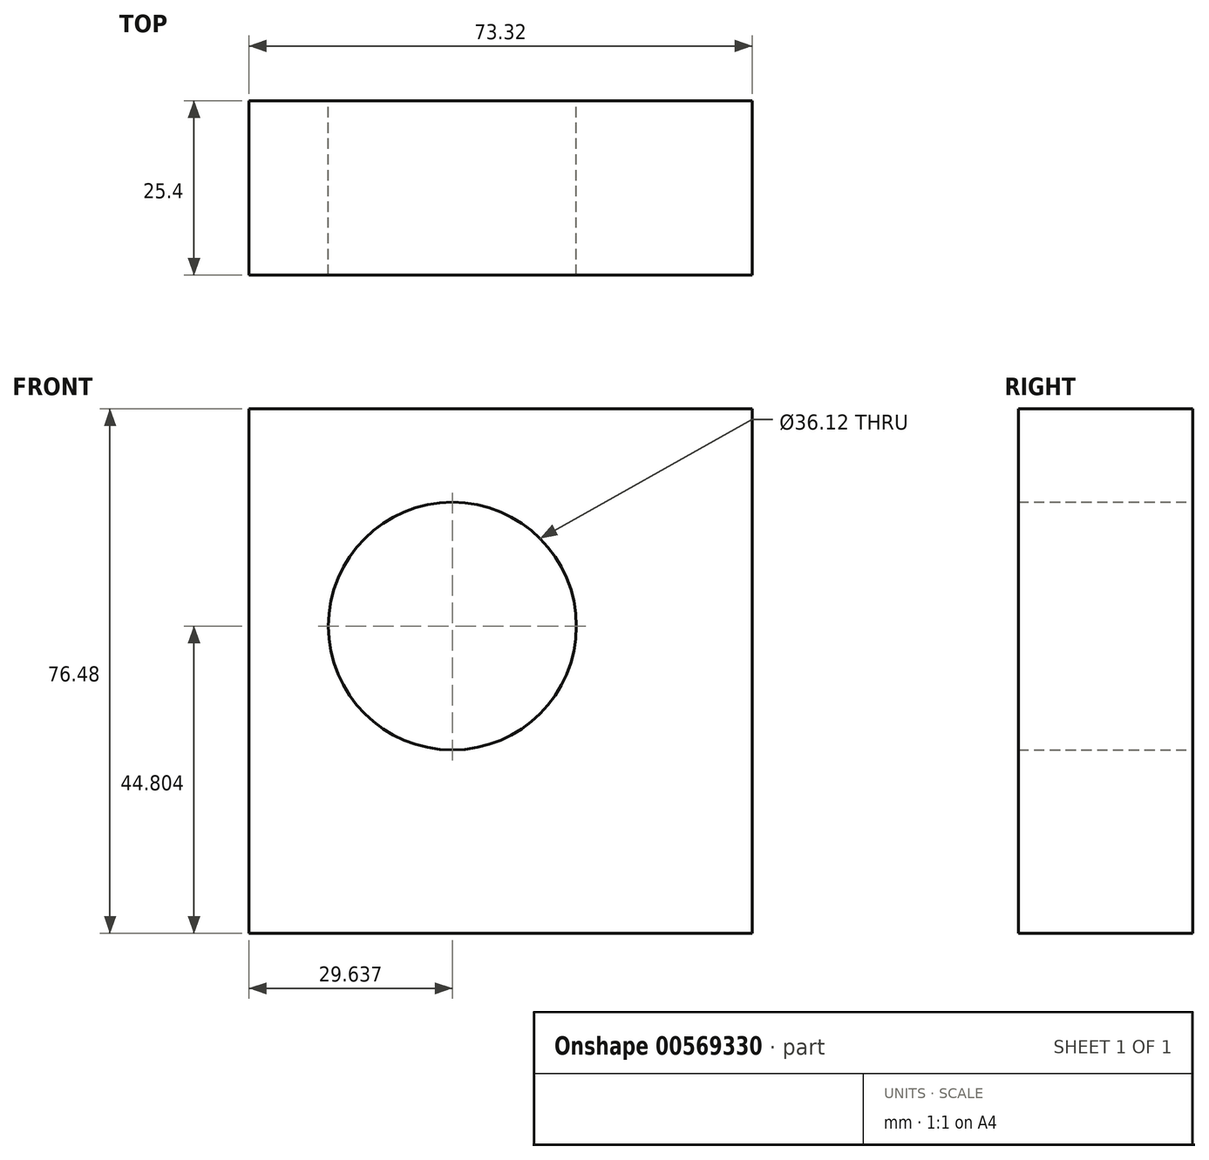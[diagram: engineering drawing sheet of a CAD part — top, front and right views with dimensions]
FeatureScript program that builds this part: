
annotation { "Feature Type Name" : "Feature", "Feature Type Description" : "" }
export const myFeature = defineFeature(function(context is Context, id is Id, definition is map)
    precondition{}
    {
        {
            var Q0;
            Q0=qCreatedBy(makeId("Front.planeOp"),FACE);
            var sketch = newSketch(context, id + "F0", { "sketchPlane" : qUnion([Q0])});
            skLineSegment(sketch, "E0.bottom", {"start": v(-49.7, 55.8) * mm, "end": v(23.62, 55.8) * mm});
            skLineSegment(sketch, "E0.top", {"start": v(-49.7, -20.68) * mm, "end": v(23.62, -20.68) * mm});
            skLineSegment(sketch, "E0.left", {"start": v(-49.7, 55.8) * mm, "end": v(-49.7, -20.68) * mm});
            skLineSegment(sketch, "E0.right", {"start": v(23.62, 55.8) * mm, "end": v(23.62, -20.68) * mm});
            skCircle(sketch, "E1", {"center": v(-20.06, 24.12) * mm, "radius": 18.06 * mm});
            skSolve(sketch);
        }
        {
            var Q0;
            Q0=makeQuery(id+"F0.imprint","IMPRINT",FACE,{"disambiguationData":[TD([[makeQuery(id+"F0.imprint","IMPRINT",EDGE,{"derivedFrom":sQuery(id+"F0.wireOp",EDGE,"E0.bottom")}),-1.0]])]});
            extrude(context, id + "F1", {"entities" : qUnion([Q0]), "depth" : 25.4 * mm, "offsetDistance" : 25.4 * mm});
        }
    });
